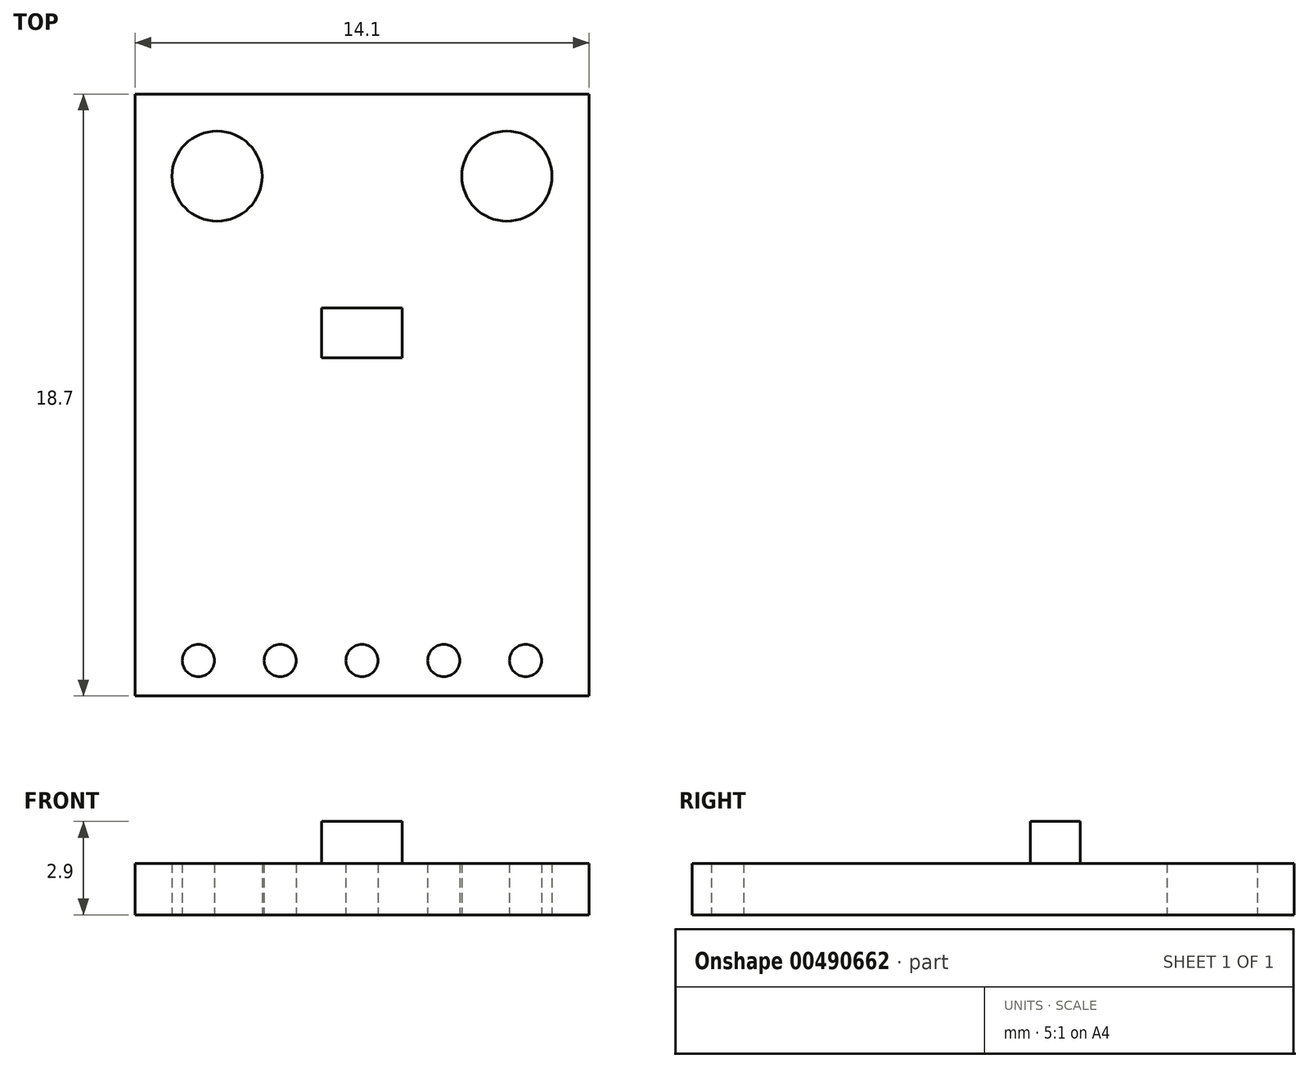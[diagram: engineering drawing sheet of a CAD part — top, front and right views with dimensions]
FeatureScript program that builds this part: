
annotation { "Feature Type Name" : "Feature", "Feature Type Description" : "" }
export const myFeature = defineFeature(function(context is Context, id is Id, definition is map)
    precondition{}
    {
        {
            var Q0;
            Q0=qCreatedBy(makeId("Top.planeOp"),FACE);
            var sketch = newSketch(context, id + "F0", { "sketchPlane" : qUnion([Q0])});
            skLineSegment(sketch, "E0.bottom", {"start": v(-7.05, 9.35) * mm, "end": v(7.05, 9.35) * mm});
            skLineSegment(sketch, "E0.top", {"start": v(-7.05, -9.35) * mm, "end": v(7.05, -9.35) * mm});
            skLineSegment(sketch, "E0.left", {"start": v(-7.05, 9.35) * mm, "end": v(-7.05, -9.35) * mm});
            skLineSegment(sketch, "E0.right", {"start": v(7.05, 9.35) * mm, "end": v(7.05, -9.35) * mm});
            skCircle(sketch, "E1", {"center": v(-4.5, 6.8) * mm, "radius": 1.4 * mm});
            skCircle(sketch, "E2", {"center": v(4.5, 6.8) * mm, "radius": 1.4 * mm});
            skCircle(sketch, "E3", {"center": v(-5.08, -8.25) * mm, "radius": 0.5 * mm});
            skCircle(sketch, "E4.1.0.0", {"center": v(-2.54, -8.25) * mm, "radius": 0.5 * mm});
            skCircle(sketch, "E4.2.0.0", {"center": v(0, -8.25) * mm, "radius": 0.5 * mm});
            skCircle(sketch, "E4.3.0.0", {"center": v(2.54, -8.25) * mm, "radius": 0.5 * mm});
            skCircle(sketch, "E4.4.0.0", {"center": v(5.08, -8.25) * mm, "radius": 0.5 * mm});
            skLineSegment(sketch, "E4.direction1", {"start": v(-5.08, -8.25) * mm, "end": v(-2.54, -8.25) * mm, "construction": true});
            skSolve(sketch);
        }
        {
            var Q0;
            Q0 = qSketchRegion(id + "F0", true);
            extrude(context, id + "F1", {"entities" : qUnion([Q0]), "depth" : 1.6 * mm});
        }
        {
            var Q0;
            Q0=makeQuery(id+"F1.opExtrude","CAP_FACE",FACE,{"disambiguationData":[OSD([sQuery(id+"F0.wireOp",EDGE,"E0.bottom"),sQuery(id+"F0.wireOp",EDGE,"E0.top"),sQuery(id+"F0.wireOp",EDGE,"E0.left"),sQuery(id+"F0.wireOp",EDGE,"E0.right"),sQuery(id+"F0.wireOp",EDGE,"E1"),sQuery(id+"F0.wireOp",EDGE,"E2")])],"isStart":false});
            var sketch = newSketch(context, id + "F2", { "sketchPlane" : qUnion([Q0])});
            skLineSegment(sketch, "E5.bottom", {"start": v(-1.25, 2.7) * mm, "end": v(1.25, 2.7) * mm});
            skLineSegment(sketch, "E5.top", {"start": v(-1.25, 1.15) * mm, "end": v(1.25, 1.15) * mm});
            skLineSegment(sketch, "E5.left", {"start": v(-1.25, 2.7) * mm, "end": v(-1.25, 1.15) * mm});
            skLineSegment(sketch, "E5.right", {"start": v(1.25, 2.7) * mm, "end": v(1.25, 1.15) * mm});
            skSolve(sketch);
        }
        {
            var Q0;
            Q0 = qSketchRegion(id + "F2", true);
            extrude(context, id + "F3", {"entities" : qUnion([Q0]), "operationType" : NewBodyOperationType.ADD, "depth" : 1.3 * mm});
        }
    });
